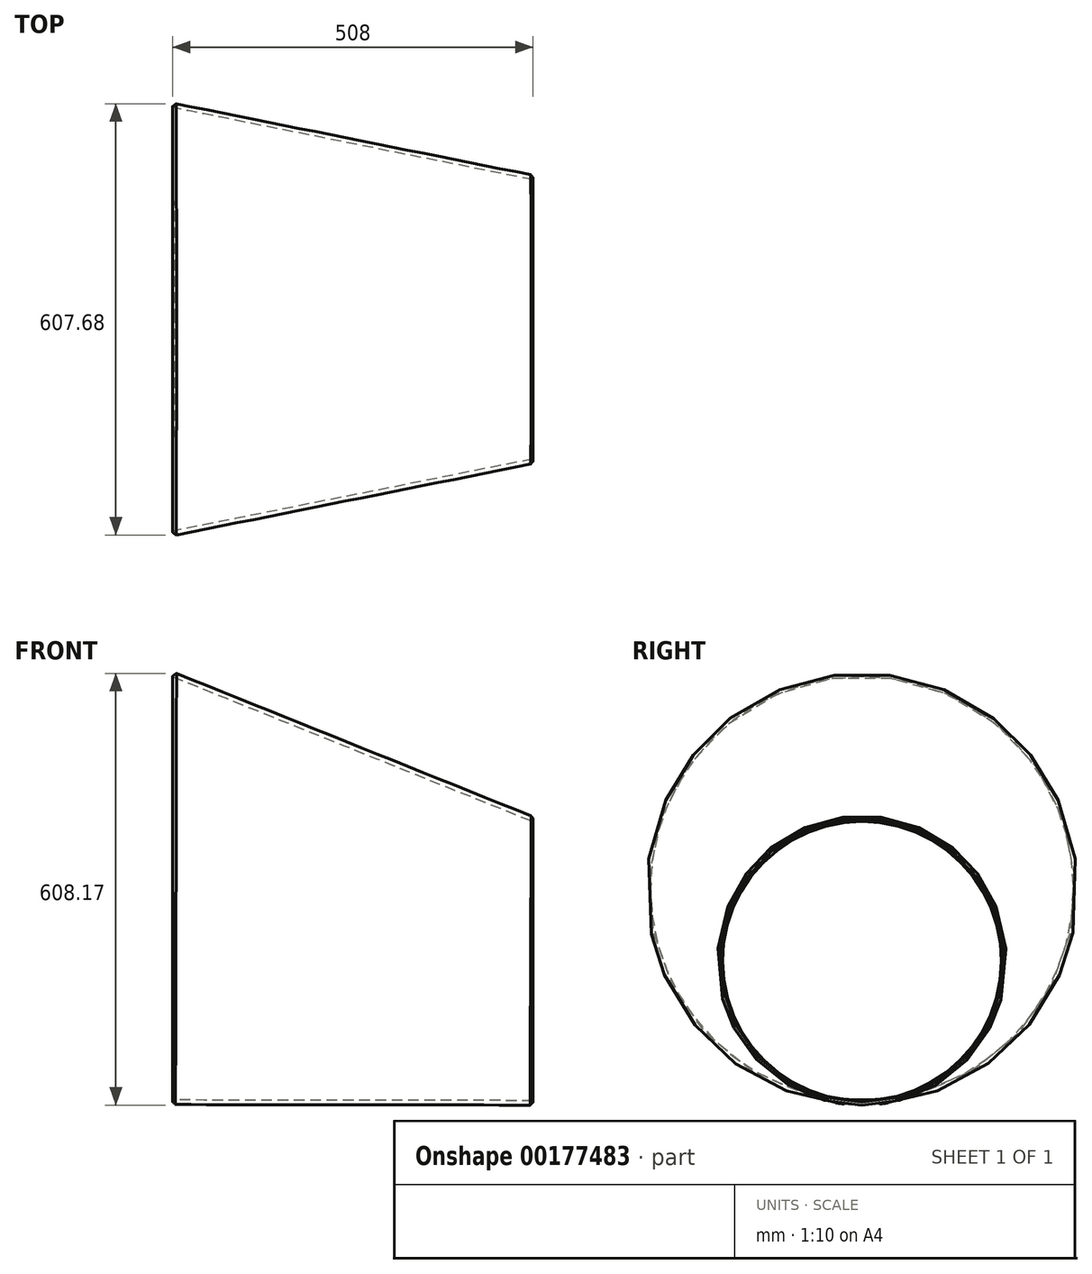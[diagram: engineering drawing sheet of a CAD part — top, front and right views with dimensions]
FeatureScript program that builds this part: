
annotation { "Feature Type Name" : "Feature", "Feature Type Description" : "" }
export const myFeature = defineFeature(function(context is Context, id is Id, definition is map)
    precondition{}
    {
        {
            var Q0;
            Q0=qCreatedBy(makeId("Front.planeOp"),FACE);
            var sketch = newSketch(context, id + "F0", { "sketchPlane" : qUnion([Q0])});
            skLineSegment(sketch, "E0", {"start": v(-257.57, -6.37) * mm, "end": v(250.43, -6.37) * mm});
            skSolve(sketch);
        }
        {
            var Q0;
            Q0=sQuery(id+"F0.wireOp",VERTEX,"E0.start");
            var Q1;
            Q1=qCreatedBy(makeId("Right.planeOp"),FACE);
            cPlane(context, id + "F1", {"entities" : qUnion([Q0, Q1]), "cplaneType" : CPlaneType.PLANE_POINT, "offset" : 25 * mm, "width" : 150 * mm, "height" : 150 * mm});
        }
        {
            var Q0;
            Q0=qCreatedBy(id+"F1.planeOp",FACE);
            var sketch = newSketch(context, id + "F2", { "sketchPlane" : qUnion([Q0])});
            skCircle(sketch, "E1", {"center": v(0, 298.43) * mm, "radius": 304.8 * mm});
            skLineSegment(sketch, "E2", {"start": v(0, 298.43) * mm, "end": v(0, -6.37) * mm, "construction": true});
            skSolve(sketch);
        }
        {
            var Q0;
            Q0=sQuery(id+"F0.wireOp",VERTEX,"E0.end");
            var Q1;
            Q1=qCreatedBy(makeId("Right.planeOp"),FACE);
            cPlane(context, id + "F3", {"entities" : qUnion([Q0, Q1]), "cplaneType" : CPlaneType.PLANE_POINT, "offset" : 25 * mm, "width" : 150 * mm, "height" : 150 * mm});
        }
        {
            var Q0;
            Q0=qCreatedBy(id+"F3.planeOp",FACE);
            var sketch = newSketch(context, id + "F4", { "sketchPlane" : qUnion([Q0])});
            skLineSegment(sketch, "E3", {"start": v(0, -7.14) * mm, "end": v(0, 196.06) * mm, "construction": true});
            skCircle(sketch, "E4", {"center": v(0, 196.06) * mm, "radius": 203.2 * mm});
            skSolve(sketch);
        }
        {
            var Q0;
            Q0=makeQuery(id+"F2.imprint","IMPRINT",FACE,{"disambiguationData":[TD([[makeQuery(id+"F2.imprint","IMPRINT",EDGE,{"derivedFrom":sQuery(id+"F2.wireOp",EDGE,"E1")}),1.0]])]});
            var Q1;
            Q1=makeQuery(id+"F4.imprint","IMPRINT",FACE,{"disambiguationData":[TD([[makeQuery(id+"F4.imprint","IMPRINT",EDGE,{"derivedFrom":sQuery(id+"F4.wireOp",EDGE,"E4")}),1.0]])]});
            loft(context, id + "F5", {"sheetProfilesArray" : [{ "sheetProfileEntities" : qUnion([Q0]) }, { "sheetProfileEntities" : qUnion([Q1]) }]});
        }
        {
            var Q0;
            Q0=makeQuery(id+"F5.opLoft","CAP_FACE",FACE,{"disambiguationData":[OSD([makeQuery(id+"F2.imprint","IMPRINT",FACE,{"disambiguationData":[TD([[makeQuery(id+"F2.imprint","IMPRINT",EDGE,{"derivedFrom":sQuery(id+"F2.wireOp",EDGE,"E1")}),1.0]])]})])],"isStart":true});
            var Q1;
            Q1=makeQuery(id+"F5.opLoft","CAP_FACE",FACE,{"disambiguationData":[OSD([makeQuery(id+"F4.imprint","IMPRINT",FACE,{"disambiguationData":[TD([[makeQuery(id+"F4.imprint","IMPRINT",EDGE,{"derivedFrom":sQuery(id+"F4.wireOp",EDGE,"E4")}),1.0]])]})])],"isStart":true});
            shell(context, id + "F6", {"entities" : qUnion([Q0, Q1]), "thickness" : 6.35 * mm});
        }
        {
            var Q0;
            Q0=makeQuery(id+"F5.opLoft","MID_CAP_EDGE",EDGE,{"disambiguationData":[OSD([sQuery(id+"F2.wireOp",EDGE,"E1")])],"capPos":0.0});
            chamfer(context, id + "F7", {"entities" : qUnion([Q0]), "width" : 4 * mm, "tangentPropagation" : true});
        }
        {
            var Q0;
            Q0=makeQuery(id+"F5.opLoft","MID_CAP_EDGE",EDGE,{"disambiguationData":[OSD([sQuery(id+"F2.wireOp",EDGE,"E1"),sQuery(id+"F4.wireOp",EDGE,"E4")])],"capPos":1.0});
            chamfer(context, id + "F8", {"entities" : qUnion([Q0]), "width" : 4 * mm, "tangentPropagation" : true});
        }
    });
